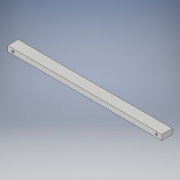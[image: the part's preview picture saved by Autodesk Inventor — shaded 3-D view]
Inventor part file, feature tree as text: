
AUTODESK INVENTOR PART (.ipt)
format: ipt  version: 2017 (Build 210142000, 142)  size: 105,984 bytes
history: native  units: in
note: dims shown in document units (in); Inventor stores cm internally (conversion verified against a paired STEP export)
features: sketch x2, extrude x1, hole x1
ambient origin geometry x8: Origin, YZ Plane, XZ Plane, XY Plane, X Axis, Y Axis, Z Axis, Center Point
bodies: Solid1 (feature_tree)
feature tree (4):
  extrude  "Extrusion1"  Depth=0.25in
  hole  "Hole1"  [1 undecoded]
  sketch  "Sketch1"  dims[d0=7.317in d1=0.25in]
  sketch  "Sketch2"  dims[d2=0.5in d3=0.0in d4=0.25in d5=0.25in d6=0.14in d7=0.14in d10=0.104in d11=0.5in d12=0.375in d13=0.25in d14=0.5635in d15=0.5in d16=0.8108in]
note: 1 required parameter value undecoded (feature->parameter linkage not recoverable at this tier; creation-order binding heuristic only, values carry confidence <= 0.55)
